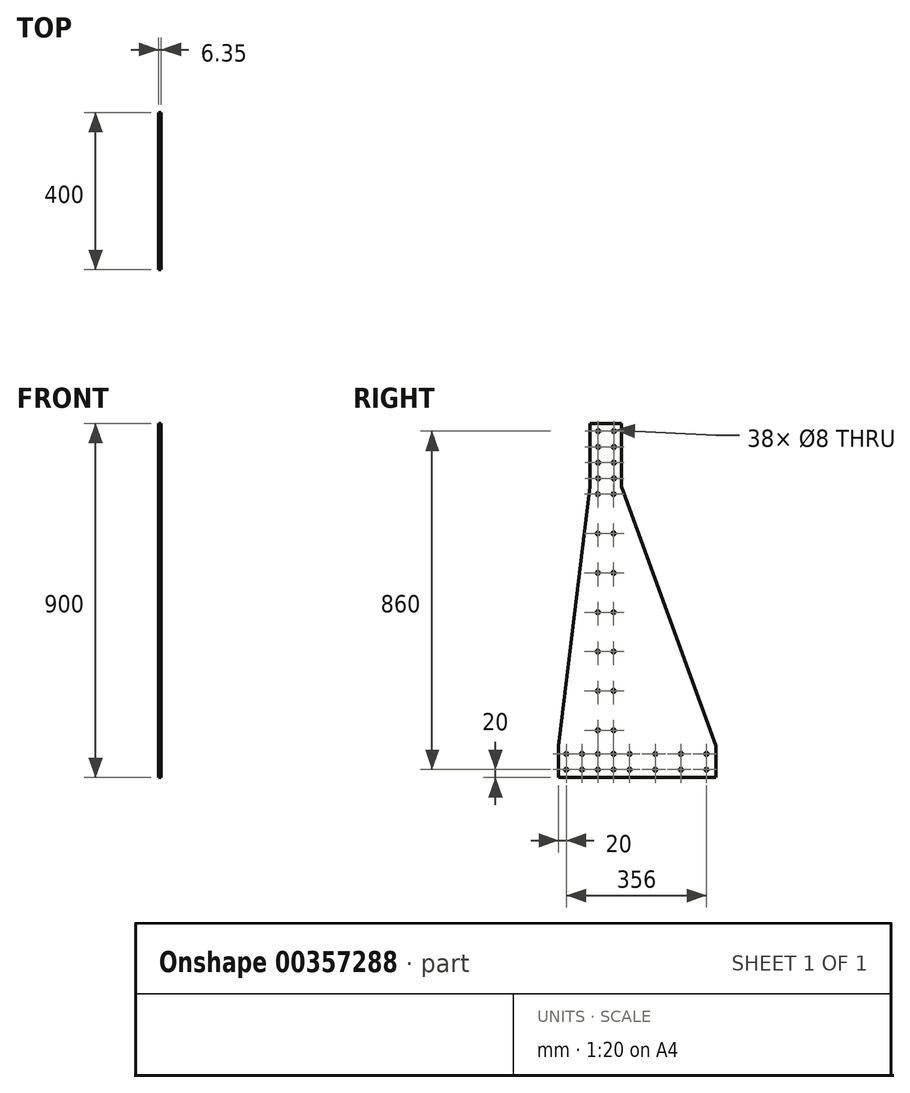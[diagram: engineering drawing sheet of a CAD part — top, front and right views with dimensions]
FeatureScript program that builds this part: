
annotation { "Feature Type Name" : "Feature", "Feature Type Description" : "" }
export const myFeature = defineFeature(function(context is Context, id is Id, definition is map)
    precondition{}
    {
        {
            var Q0;
            Q0=qCreatedBy(makeId("Right.planeOp"),FACE);
            var sketch = newSketch(context, id + "F0", { "sketchPlane" : qUnion([Q0])});
            skLineSegment(sketch, "E0", {"start": v(0, 0) * mm, "end": v(0, 900) * mm, "construction": true});
            skLineSegment(sketch, "E1", {"start": v(0, 0) * mm, "end": v(280, 0) * mm});
            skLineSegment(sketch, "E2.0", {"start": v(40, 740) * mm, "end": v(40, 900) * mm});
            skLineSegment(sketch, "E3.0", {"start": v(-40, 740) * mm, "end": v(-40, 900) * mm});
            skLineSegment(sketch, "E4", {"start": v(0, 0) * mm, "end": v(-120, 0) * mm});
            skLineSegment(sketch, "E5", {"start": v(280, 0) * mm, "end": v(280, 80) * mm});
            skLineSegment(sketch, "E6", {"start": v(-120, 80) * mm, "end": v(-120, 0) * mm});
            skLineSegment(sketch, "E7", {"start": v(-40, 900) * mm, "end": v(40, 900) * mm});
            skLineSegment(sketch, "E8", {"start": v(40, 740) * mm, "end": v(280, 80) * mm});
            skLineSegment(sketch, "E9", {"start": v(-40, 740) * mm, "end": v(-120, 80) * mm});
            skSolve(sketch);
        }
        {
            var Q0;
            Q0 = qSketchRegion(id + "F0", true);
            extrude(context, id + "F1", {"entities" : qUnion([Q0]), "depth" : 6.35 * mm});
        }
        {
            var Q0;
            Q0=makeQuery(id+"F1.opExtrude","CAP_FACE",FACE,{"disambiguationData":[OSD([sQuery(id+"F0.wireOp",EDGE,"E1"),sQuery(id+"F0.wireOp",EDGE,"E2.0"),sQuery(id+"F0.wireOp",EDGE,"E3.0"),sQuery(id+"F0.wireOp",EDGE,"E4"),sQuery(id+"F0.wireOp",EDGE,"E5"),sQuery(id+"F0.wireOp",EDGE,"E6"),sQuery(id+"F0.wireOp",EDGE,"E7"),sQuery(id+"F0.wireOp",EDGE,"E8"),sQuery(id+"F0.wireOp",EDGE,"E9")])],"isStart":false});
            var sketch = newSketch(context, id + "F2", { "sketchPlane" : qUnion([Q0])});
            skCircle(sketch, "E10", {"center": v(-19, 880) * mm, "radius": 4 * mm});
            skCircle(sketch, "E11.0.1.0", {"center": v(-19, 800) * mm, "radius": 4 * mm});
            skLineSegment(sketch, "E11.direction2", {"start": v(-19, 880) * mm, "end": v(-19, 800) * mm, "construction": true});
            skCircle(sketch, "E12.0.1.0", {"center": v(-19, 840) * mm, "radius": 4 * mm});
            skCircle(sketch, "E12.0.1.1", {"center": v(-19, 760) * mm, "radius": 4 * mm});
            skCircle(sketch, "E12.1.0.0", {"center": v(21, 880) * mm, "radius": 4 * mm});
            skCircle(sketch, "E12.1.0.1", {"center": v(21, 800) * mm, "radius": 4 * mm});
            skCircle(sketch, "E12.1.1.0", {"center": v(21, 840) * mm, "radius": 4 * mm});
            skCircle(sketch, "E12.1.1.1", {"center": v(21, 760) * mm, "radius": 4 * mm});
            skLineSegment(sketch, "E12.direction1", {"start": v(-19, 800) * mm, "end": v(21, 800) * mm, "construction": true});
            skLineSegment(sketch, "E12.direction2", {"start": v(-19, 800) * mm, "end": v(-19, 760) * mm, "construction": true});
            skCircle(sketch, "E13", {"center": v(-100, 20) * mm, "radius": 4 * mm});
            skCircle(sketch, "E14.0.1.0", {"center": v(-100, 60) * mm, "radius": 4 * mm});
            skCircle(sketch, "E14.1.0.0", {"center": v(-60, 20) * mm, "radius": 4 * mm});
            skCircle(sketch, "E14.1.1.0", {"center": v(-60, 60) * mm, "radius": 4 * mm});
            skLineSegment(sketch, "E14.direction1", {"start": v(-100, 20) * mm, "end": v(-60, 20) * mm, "construction": true});
            skLineSegment(sketch, "E14.direction2", {"start": v(-100, 20) * mm, "end": v(-100, 60) * mm, "construction": true});
            skCircle(sketch, "E15", {"center": v(256, 20) * mm, "radius": 4 * mm});
            skCircle(sketch, "E16.0.1.0", {"center": v(256, 60) * mm, "radius": 4 * mm});
            skCircle(sketch, "E16.1.0.0", {"center": v(191, 20) * mm, "radius": 4 * mm});
            skCircle(sketch, "E16.1.1.0", {"center": v(191, 60) * mm, "radius": 4 * mm});
            skCircle(sketch, "E16.2.0.0", {"center": v(126, 20) * mm, "radius": 4 * mm});
            skCircle(sketch, "E16.2.1.0", {"center": v(126, 60) * mm, "radius": 4 * mm});
            skCircle(sketch, "E16.3.0.0", {"center": v(61, 20) * mm, "radius": 4 * mm});
            skCircle(sketch, "E16.3.1.0", {"center": v(61, 60) * mm, "radius": 4 * mm});
            skLineSegment(sketch, "E16.direction1", {"start": v(256, 20) * mm, "end": v(191, 20) * mm, "construction": true});
            skLineSegment(sketch, "E16.direction2", {"start": v(256, 20) * mm, "end": v(256, 60) * mm, "construction": true});
            skLineSegment(sketch, "E17", {"start": v(0, 900) * mm, "end": v(0, 0) * mm, "construction": true});
            skCircle(sketch, "E18", {"center": v(20, 20) * mm, "radius": 4 * mm});
            skCircle(sketch, "E19.0.1.0", {"center": v(20, 120) * mm, "radius": 4 * mm});
            skCircle(sketch, "E19.0.2.0", {"center": v(20, 220) * mm, "radius": 4 * mm});
            skCircle(sketch, "E19.0.3.0", {"center": v(20, 320) * mm, "radius": 4 * mm});
            skCircle(sketch, "E19.0.4.0", {"center": v(20, 420) * mm, "radius": 4 * mm});
            skCircle(sketch, "E19.0.5.0", {"center": v(20, 520) * mm, "radius": 4 * mm});
            skCircle(sketch, "E19.0.6.0", {"center": v(20, 620) * mm, "radius": 4 * mm});
            skCircle(sketch, "E19.0.7.0", {"center": v(20, 720) * mm, "radius": 4 * mm});
            skCircle(sketch, "E19.1.0.0", {"center": v(-20, 20) * mm, "radius": 4 * mm});
            skCircle(sketch, "E19.1.1.0", {"center": v(-20, 120) * mm, "radius": 4 * mm});
            skCircle(sketch, "E19.1.2.0", {"center": v(-20, 220) * mm, "radius": 4 * mm});
            skCircle(sketch, "E19.1.3.0", {"center": v(-20, 320) * mm, "radius": 4 * mm});
            skCircle(sketch, "E19.1.4.0", {"center": v(-20, 420) * mm, "radius": 4 * mm});
            skCircle(sketch, "E19.1.5.0", {"center": v(-20, 520) * mm, "radius": 4 * mm});
            skCircle(sketch, "E19.1.6.0", {"center": v(-20, 620) * mm, "radius": 4 * mm});
            skCircle(sketch, "E19.1.7.0", {"center": v(-20, 720) * mm, "radius": 4 * mm});
            skLineSegment(sketch, "E19.direction1", {"start": v(20, 20) * mm, "end": v(-20, 20) * mm, "construction": true});
            skLineSegment(sketch, "E19.direction2", {"start": v(20, 20) * mm, "end": v(20, 120) * mm, "construction": true});
            skCircle(sketch, "E20.0.1.0", {"center": v(20, 60) * mm, "radius": 4 * mm});
            skCircle(sketch, "E20.0.1.1", {"center": v(-20, 60) * mm, "radius": 4 * mm});
            skLineSegment(sketch, "E20.direction1", {"start": v(-20, 20) * mm, "end": v(5, 20) * mm, "construction": true});
            skLineSegment(sketch, "E20.direction2", {"start": v(-20, 20) * mm, "end": v(-20, 60) * mm, "construction": true});
            skSolve(sketch);
        }
        {
            var Q0;
            Q0 = qSketchRegion(id + "F2", true);
            extrude(context, id + "F3", {"entities" : qUnion([Q0]), "operationType" : NewBodyOperationType.REMOVE, "endBound" : BoundingType.THROUGH_ALL, "oppositeDirection" : true, "depth" : 25 * mm});
        }
    });
